# Revit family: Lintel_StandardLoad_KeystoneLintelsLtd_BOXK_2D
name_source: partatom
category: Detail Items
revit_build: Autodesk Revit 2015 (Build: 20160512_1515(x64)
units: mm (PartAtom-declared; Revit-internal decimal feet)

## types (4) — shared parameters
Assembly Code = B20
AssetType = Fixed
BIMObjectName = Lintel_StandardLoad_KeystoneLintelsLtd_BOXK_2D
ClassificationName = Uniclass2015
ClassificationValue = Pr_20_85_48_11
Color = Silver
DurationUnit = Years
ExpectedLife = 55
IfcExportAs = IfcBeam
IfcExportType = IfcBeamTypeEnum.LINTEL
Keynote = L
Manufacturer = Keystone Lintels Ltd
ManufacturerName = Keystone Lintels Ltd
Model = Standard Load - BOX/K
ModelReference = Standard Load - BOX/K
NBSDescription = Prefabricated steel lintels
NBSObjectName = Keystone Lintels Ltd - Prefabricated steel lintels
NBSReference = 45-80-50/406
ProductionYear = 2017
TypeName = Standard Load - BOX/K
URL = http://keystonelintels.com
WarrantyDurationUnit = Years
_BSBibleVersion = 14
_CurrentRevision = 1
_DistributedBy = www.bimstore.co.uk
zero-valued in all types: Cost, NominalDepth, NominalHeight, NominalLength, _BimSpecGuid

## per-type parameters (varying)
| type | 075 | 100 | 140 | 200 | CavityWidth | Description | Features |
| BOX/K - 200 | No | No | No | Yes | 200 mm  [stored 0.656168 ft] | Used to support openings in 200mm wide walls. Steel Lintels may be propped to facilitate speed of construction. | Used to support openings in 200mm wide walls. Steel Lintels may be propped to facilitate speed of construction. |
| BOX/K - 140 | No | No | Yes | No | 145 mm  [stored 0.475722 ft] | Used to support openings in 150mm wide walls. Steel Lintels may be propped to facilitate speed of construction. | Used to support openings in 150mm wide walls. Steel Lintels may be propped to facilitate speed of construction. |
| BOX/K - 100 | No | Yes | No | No | 95 mm | Used to support openings in 100mm wide walls. Steel Lintels may be propped to facilitate speed of construction. | Used to support openings in 100mm wide walls. Steel Lintels may be propped to facilitate speed of construction. |
| BOX/K - 75 | Yes | No | No | No | 95 mm | Used to support openings in 100mm wide walls. Steel Lintels may be propped to facilitate speed of construction. | Used to support openings in 100mm wide walls. Steel Lintels may be propped to facilitate speed of construction. |

note: column(s) folded — value = type name in every type: ModelNumber, ProductCode, Size, Type Comments

note: [stored X ft] marks values corroborated as IEEE doubles in the binary element streams (Revit-internal decimal feet)

## geometry (parser evidence)
native form markers: Blend x4, Sweep x5
no freeform markers — native parametric forms only
